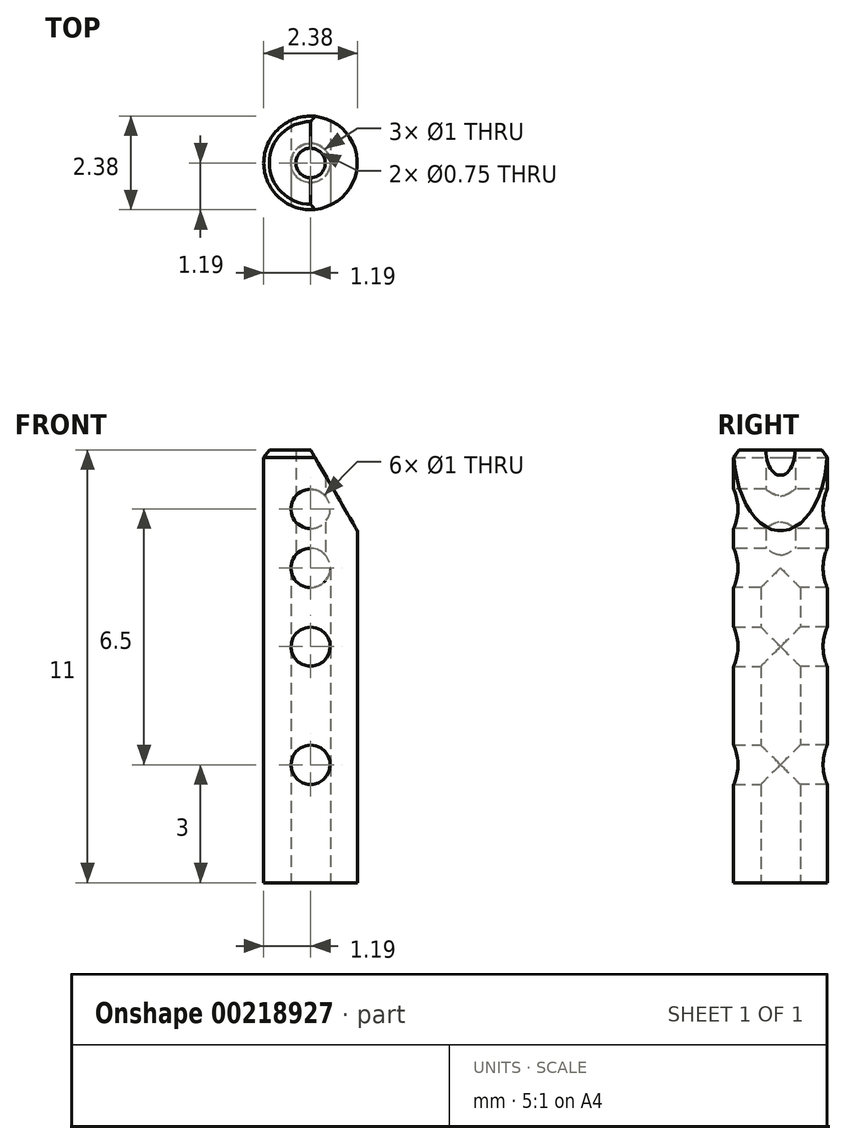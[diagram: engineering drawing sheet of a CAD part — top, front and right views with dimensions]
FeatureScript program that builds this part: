
annotation { "Feature Type Name" : "Feature", "Feature Type Description" : "" }
export const myFeature = defineFeature(function(context is Context, id is Id, definition is map)
    precondition{}
    {
        {
            var Q0;
            Q0=qCreatedBy(makeId("Right.planeOp"),FACE);
            var sketch = newSketch(context, id + "F0", { "sketchPlane" : qUnion([Q0])});
            skLineSegment(sketch, "E0", {"start": v(0, 0) * mm, "end": v(0, 11) * mm});
            skLineSegment(sketch, "E1", {"start": v(0, 11) * mm, "end": v(-1.05, 11) * mm});
            skLineSegment(sketch, "E2", {"start": v(-1.2, 10.8) * mm, "end": v(-1.19, 0) * mm});
            skLineSegment(sketch, "E3", {"start": v(-1.19, 0) * mm, "end": v(0, 0) * mm});
            skLineSegment(sketch, "E4", {"start": v(-1.05, 11) * mm, "end": v(-1.2, 10.8) * mm});
            skSolve(sketch);
        }
        {
            var Q0;
            Q0=makeQuery(id+"F0.imprint","IMPRINT",FACE,{"disambiguationData":[TD([[makeQuery(id+"F0.imprint","IMPRINT",EDGE,{"derivedFrom":sQuery(id+"F0.wireOp",EDGE,"E0")}),1.0]])]});
            var Q1;
            Q1=sQuery(id+"F0.wireOp",EDGE,"E0");
            revolve(context, id + "F1", {"entities" : qUnion([Q0]), "axis" : qUnion([Q1]), "revolveType" : RevolveType.FULL});
        }
        {
            var Q0;
            Q0=qCreatedBy(makeId("Top.planeOp"),FACE);
            var sketch = newSketch(context, id + "F2", { "sketchPlane" : qUnion([Q0])});
            skCircle(sketch, "E5", {"center": v(0, 0) * mm, "radius": 0.37 * mm});
            skSolve(sketch);
        }
        {
            var Q0;
            Q0 = qSketchRegion(id + "F2", true);
            extrude(context, id + "F3", {"entities" : qUnion([Q0]), "operationType" : NewBodyOperationType.REMOVE, "depth" : 100 * mm});
        }
        {
            var Q0;
            Q0=makeQuery(id+"F1.opRevolve","SWEPT_FACE",FACE,{"disambiguationData":[OSD([sQuery(id+"F0.wireOp",EDGE,"E3")])]});
            var sketch = newSketch(context, id + "F4", { "sketchPlane" : qUnion([Q0])});
            skCircle(sketch, "E6", {"center": v(0, 0) * mm, "radius": 0.5 * mm});
            skSolve(sketch);
        }
        {
            var Q0;
            Q0 = qSketchRegion(id + "F4", true);
            extrude(context, id + "F5", {"entities" : qUnion([Q0]), "operationType" : NewBodyOperationType.REMOVE, "oppositeDirection" : true, "depth" : 8 * mm});
        }
        {
            var Q0;
            Q0=qCreatedBy(makeId("Front.planeOp"),FACE);
            var sketch = newSketch(context, id + "F6", { "sketchPlane" : qUnion([Q0])});
            skCircle(sketch, "E7", {"center": v(0, 20.84) * mm, "radius": 0.71 * mm});
            skCircle(sketch, "E8", {"center": v(0, 9.5) * mm, "radius": 0.5 * mm});
            skCircle(sketch, "E9", {"center": v(0, 8) * mm, "radius": 0.5 * mm});
            skCircle(sketch, "E10", {"center": v(0, 6) * mm, "radius": 0.5 * mm});
            skCircle(sketch, "E11", {"center": v(0, 3) * mm, "radius": 0.5 * mm});
            skCircle(sketch, "E12", {"center": v(0, 12.5) * mm, "radius": 0.5 * mm});
            skSolve(sketch);
        }
        {
            var Q0;
            Q0 = qSketchRegion(id + "F6", true);
            extrude(context, id + "F7", {"entities" : qUnion([Q0]), "operationType" : NewBodyOperationType.REMOVE, "oppositeDirection" : true, "depth" : 25 * mm});
        }
        {
            var Q0;
            Q0 = qSketchRegion(id + "F6", true);
            extrude(context, id + "F8", {"entities" : qUnion([Q0]), "operationType" : NewBodyOperationType.REMOVE, "depth" : 25 * mm});
        }
        {
            var Q0;
            Q0=qCreatedBy(makeId("Front.planeOp"),FACE);
            var sketch = newSketch(context, id + "F9", { "sketchPlane" : qUnion([Q0])});
            skLineSegment(sketch, "E13", {"start": v(0, 11) * mm, "end": v(1.58, 11) * mm});
            skLineSegment(sketch, "E14", {"start": v(1.58, 11) * mm, "end": v(1.58, 8.26) * mm});
            skLineSegment(sketch, "E15", {"start": v(1.58, 8.26) * mm, "end": v(0, 11) * mm});
            skSolve(sketch);
        }
        {
            var Q0;
            Q0 = qSketchRegion(id + "F9", true);
            extrude(context, id + "F10", {"entities" : qUnion([Q0]), "operationType" : NewBodyOperationType.REMOVE, "oppositeDirection" : true, "depth" : 5 * mm});
        }
        {
            var Q0;
            Q0 = qSketchRegion(id + "F9", true);
            extrude(context, id + "F11", {"entities" : qUnion([Q0]), "operationType" : NewBodyOperationType.REMOVE, "depth" : 25 * mm});
        }
    });
